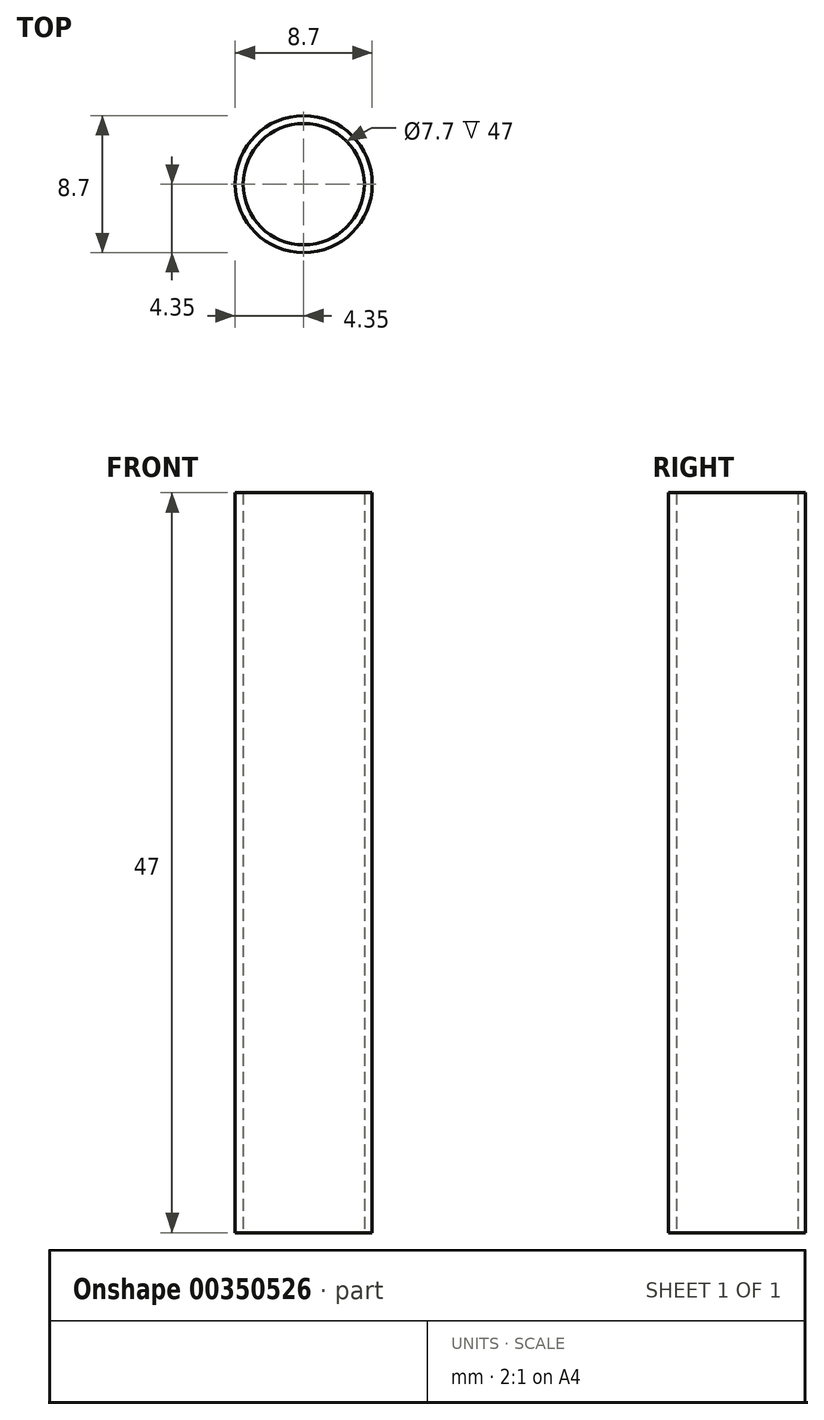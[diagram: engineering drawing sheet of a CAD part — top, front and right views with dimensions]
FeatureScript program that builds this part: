
annotation { "Feature Type Name" : "Feature", "Feature Type Description" : "" }
export const myFeature = defineFeature(function(context is Context, id is Id, definition is map)
    precondition{}
    {
        {
            var Q0;
            Q0=qCreatedBy(makeId("Top.planeOp"),FACE);
            var sketch = newSketch(context, id + "F0", { "sketchPlane" : qUnion([Q0])});
            skCircle(sketch, "E0", {"center": v(0, 0) * mm, "radius": 3.85 * mm});
            skCircle(sketch, "E1", {"center": v(0, 0) * mm, "radius": 4.35 * mm});
            skSolve(sketch);
        }
        {
            var Q0;
            Q0 = qSketchRegion(id + "F0", true);
            extrude(context, id + "F1", {"entities" : qUnion([Q0]), "depth" : 47 * mm});
        }
    });
